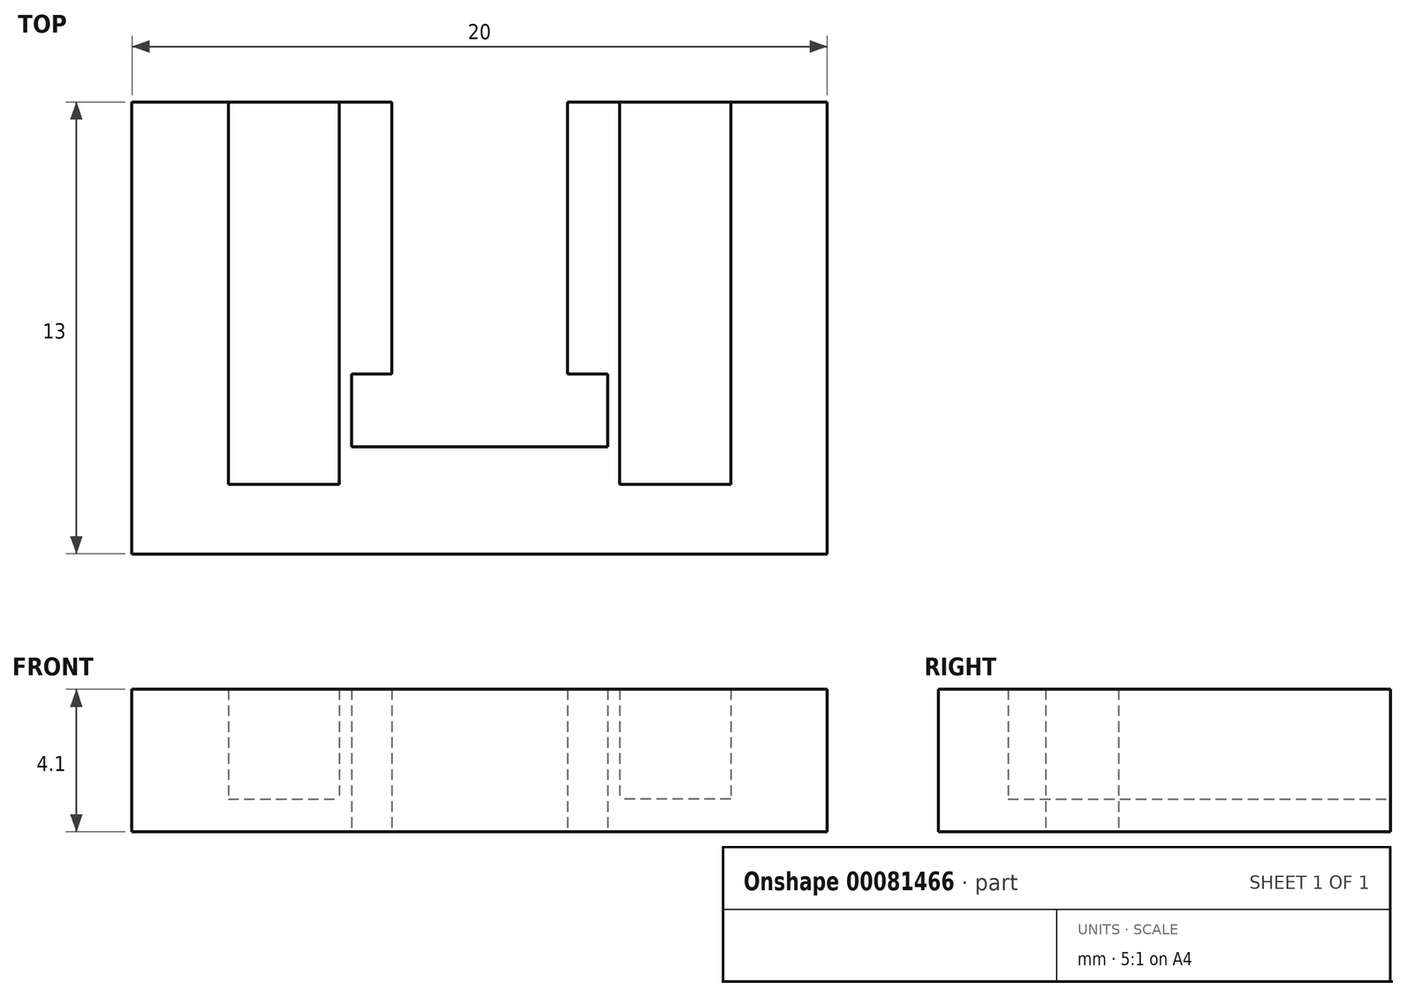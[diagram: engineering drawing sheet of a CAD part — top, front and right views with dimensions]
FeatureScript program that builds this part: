
annotation { "Feature Type Name" : "Feature", "Feature Type Description" : "" }
export const myFeature = defineFeature(function(context is Context, id is Id, definition is map)
    precondition{}
    {
        {
            var Q0;
            Q0=qCreatedBy(makeId("Top.planeOp"),FACE);
            var sketch = newSketch(context, id + "F0", { "sketchPlane" : qUnion([Q0])});
            skLineSegment(sketch, "E0.bottom", {"start": v(-25.32, -0.2) * mm, "end": v(-5.32, -0.2) * mm});
            skLineSegment(sketch, "E0.top", {"start": v(-25.32, -13.2) * mm, "end": v(-5.32, -13.2) * mm});
            skLineSegment(sketch, "E0.left", {"start": v(-25.32, -0.2) * mm, "end": v(-25.32, -13.2) * mm});
            skLineSegment(sketch, "E0.right", {"start": v(-5.32, -0.2) * mm, "end": v(-5.32, -13.2) * mm});
            skLineSegment(sketch, "E1", {"start": v(-15.32, -0.2) * mm, "end": v(-17.85, -0.2) * mm});
            skLineSegment(sketch, "E2", {"start": v(-15.32, -0.2) * mm, "end": v(-12.8, -0.2) * mm});
            skLineSegment(sketch, "E3", {"start": v(-17.85, -0.2) * mm, "end": v(-17.85, -8.02) * mm});
            skLineSegment(sketch, "E4", {"start": v(-17.85, -8.02) * mm, "end": v(-19, -8.02) * mm});
            skLineSegment(sketch, "E5", {"start": v(-19, -8.02) * mm, "end": v(-19, -10.12) * mm});
            skLineSegment(sketch, "E6", {"start": v(-19, -10.12) * mm, "end": v(-11.64, -10.12) * mm});
            skLineSegment(sketch, "E7", {"start": v(-11.64, -10.12) * mm, "end": v(-11.64, -8.02) * mm});
            skLineSegment(sketch, "E8", {"start": v(-11.64, -8.02) * mm, "end": v(-12.8, -8.02) * mm});
            skLineSegment(sketch, "E9", {"start": v(-12.8, -0.2) * mm, "end": v(-12.8, -8.02) * mm});
            skSolve(sketch);
        }
        {
            var Q0;
            Q0=makeQuery(id+"F0.imprint","IMPRINT",FACE,{"disambiguationData":[TD([[makeQuery(id+"F0.imprint","IMPRINT",EDGE,{"derivedFrom":sQuery(id+"F0.wireOp",EDGE,"E0.top")}),1.0]])]});
            var Q1;
            Q1 = qSketchRegion(id + "F3", true);
            var Q2;
            Q2 = qSketchRegion(id + "F2", true);
            extrude(context, id + "F1", {"entities" : qUnion([Q0, Q1, Q2]), "depth" : 5.1 * mm});
        }
        {
            var Q0;
            {var subQ0=sQuery(id+"F0.wireOp",EDGE,"E0.bottom");Q0=makeQuery(id+"F1.opExtrude","SWEPT_FACE",FACE,{"disambiguationData":[OSD([subQ0]),TDD([makeQuery(id+"F0.imprint","IMPRINT",EDGE,{"disambiguationData":[TD([[makeQuery(id+"F0.imprint","INTERSECT",VERTEX,{"derivedFrom":[subQ0,sQuery(id+"F0.wireOp",EDGE,"E0.right")]}),1.0]])],"derivedFrom":subQ0})])]});}
            var sketch = newSketch(context, id + "F2", { "sketchPlane" : qUnion([Q0])});
            skLineSegment(sketch, "E10", {"start": v(11.3, 4.15) * mm, "end": v(8.1, 4.15) * mm});
            skLineSegment(sketch, "E11", {"start": v(8.1, 4.15) * mm, "end": v(8.1, 0.95) * mm});
            skLineSegment(sketch, "E12", {"start": v(8.1, 0.95) * mm, "end": v(11.3, 0.95) * mm});
            skLineSegment(sketch, "E13", {"start": v(11.3, 4.15) * mm, "end": v(11.3, 0.95) * mm});
            skSolve(sketch);
        }
        {
            var Q0;
            {var subQ0=sQuery(id+"F0.wireOp",EDGE,"E0.bottom");Q0=makeQuery(id+"F1.opExtrude","SWEPT_FACE",FACE,{"disambiguationData":[OSD([subQ0]),TDD([makeQuery(id+"F0.imprint","IMPRINT",EDGE,{"disambiguationData":[TD([[makeQuery(id+"F0.imprint","INTERSECT",VERTEX,{"derivedFrom":[subQ0,sQuery(id+"F0.wireOp",EDGE,"E0.left")]}),-1.0]])],"derivedFrom":subQ0})])]});}
            var sketch = newSketch(context, id + "F3", { "sketchPlane" : qUnion([Q0])});
            skLineSegment(sketch, "E14", {"start": v(19.35, 4.15) * mm, "end": v(22.55, 4.15) * mm});
            skLineSegment(sketch, "E15", {"start": v(22.55, 4.15) * mm, "end": v(22.55, 0.95) * mm});
            skLineSegment(sketch, "E16", {"start": v(22.55, 0.95) * mm, "end": v(19.35, 0.95) * mm});
            skLineSegment(sketch, "E17", {"start": v(19.35, 4.15) * mm, "end": v(19.35, 0.95) * mm});
            skSolve(sketch);
        }
        {
            var Q0;
            Q0=makeQuery(id+"F2.imprint","IMPRINT",FACE,{"disambiguationData":[TD([[makeQuery(id+"F2.imprint","IMPRINT",EDGE,{"derivedFrom":sQuery(id+"F2.wireOp",EDGE,"E10")}),1.0]])]});
            extrude(context, id + "F4", {"entities" : qUnion([Q0]), "operationType" : NewBodyOperationType.REMOVE, "oppositeDirection" : true, "depth" : 11 * mm});
        }
        {
            var Q0;
            Q0 = qSketchRegion(id + "F3", true);
            extrude(context, id + "F5", {"entities" : qUnion([Q0]), "operationType" : NewBodyOperationType.REMOVE, "oppositeDirection" : true, "depth" : 11 * mm});
        }
        {
            var Q0;
            Q0=makeQuery(id+"F1.opExtrude","CAP_FACE",FACE,{"disambiguationData":[OSD([sQuery(id+"F0.wireOp",EDGE,"E0.bottom"),sQuery(id+"F0.wireOp",EDGE,"E0.top"),sQuery(id+"F0.wireOp",EDGE,"E0.left"),sQuery(id+"F0.wireOp",EDGE,"E0.right"),sQuery(id+"F0.wireOp",EDGE,"E3"),sQuery(id+"F0.wireOp",EDGE,"E4"),sQuery(id+"F0.wireOp",EDGE,"E5"),sQuery(id+"F0.wireOp",EDGE,"E6"),sQuery(id+"F0.wireOp",EDGE,"E7"),sQuery(id+"F0.wireOp",EDGE,"E8"),sQuery(id+"F0.wireOp",EDGE,"E9")])],"isStart":false});
            extrude(context, id + "F6", {"entities" : qUnion([Q0]), "operationType" : NewBodyOperationType.REMOVE, "oppositeDirection" : true, "depth" : 1 * mm});
        }
    });
